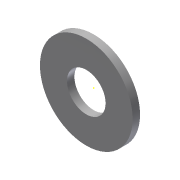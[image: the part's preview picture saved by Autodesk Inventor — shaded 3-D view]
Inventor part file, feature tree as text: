
AUTODESK INVENTOR PART (.ipt)
format: ipt  version: 2013 (Build 170138000, 138)  size: 88,576 bytes
history: native  units: in
note: dims shown in document units (in); Inventor stores cm internally (conversion verified against a paired STEP export)
features: sketch x2, extrude x1
ambient origin geometry x8: Origin, YZ Plane, XZ Plane, XY Plane, X Axis, Y Axis, Z Axis, Center Point
bodies: Solid1 (feature_tree)
feature tree (3):
  sketch  "Sketch1"  dims[d0=0.3125in d1=0.75in]
  extrude  "Extrusion1"  Depth=0.75in
  sketch  "Sketch2"  dims[d2=0.06in d3=0.0in]
